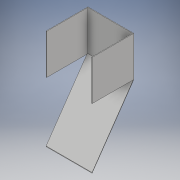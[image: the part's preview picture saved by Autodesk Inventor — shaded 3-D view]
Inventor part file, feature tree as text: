
AUTODESK INVENTOR PART (.ipt)
format: ipt  version: 2018 (Build 220112000, 112)  size: 119,808 bytes
history: native  units: mm
features: extrude x2, sketch x2
ambient origin geometry x8: Origin, YZ Plane, XZ Plane, XY Plane, X Axis, Y Axis, Z Axis, Center Point
bodies: Solid1 (feature_tree)
feature tree (4):
  extrude  "Extrusion1"  Depth=77.0mm
  extrude  "Extrusion2"  Depth=1.0mm
  sketch  "Sketch1"  dims[d0=70.0mm d1=77.0mm]
  sketch  "Sketch2"  dims[d3=70.0mm d5=1.0mm d6=69.0mm d7=90.0deg d8=75.0mm d9=90.0deg d10=69.0mm d11=90.0deg d12=1.0mm d13=67.0mm d14=0.0mm d15=1.0mm d16=90.0deg d17=1.0mm d18=0.0mm d19=77.0mm d20=0.0mm]
